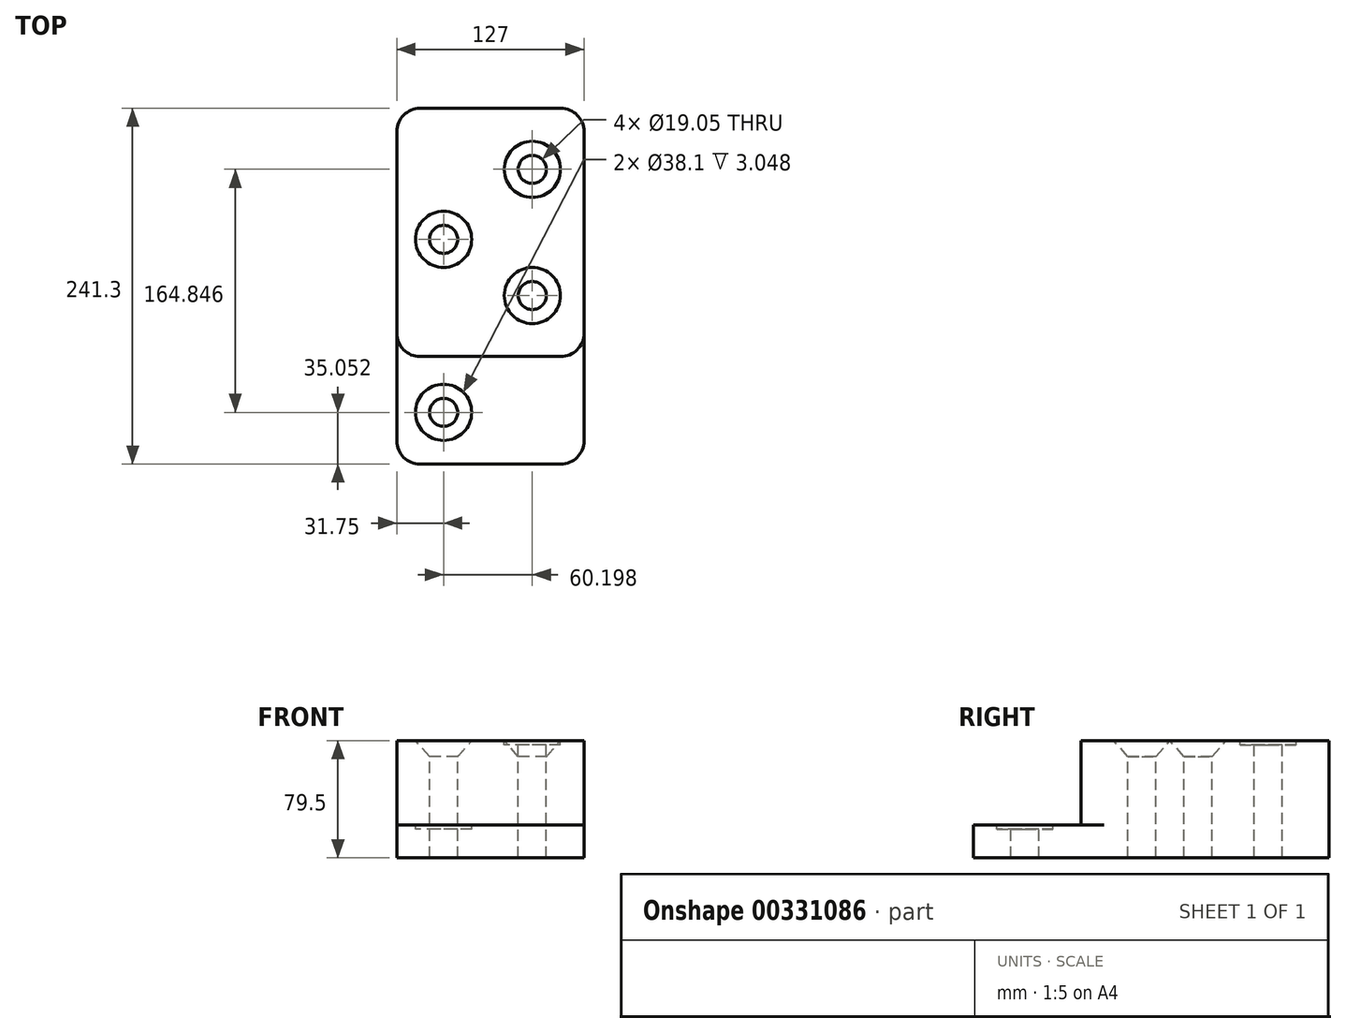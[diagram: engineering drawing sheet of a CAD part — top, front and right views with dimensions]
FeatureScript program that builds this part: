
annotation { "Feature Type Name" : "Feature", "Feature Type Description" : "" }
export const myFeature = defineFeature(function(context is Context, id is Id, definition is map)
    precondition{}
    {
        {
            var Q0;
            Q0=qCreatedBy(makeId("Top.planeOp"),FACE);
            var sketch = newSketch(context, id + "F0", { "sketchPlane" : qUnion([Q0])});
            skLineSegment(sketch, "E0.bottom", {"start": v(0, 0) * mm, "end": v(127, 0) * mm});
            skLineSegment(sketch, "E0.top", {"start": v(0, 241.3) * mm, "end": v(127, 241.3) * mm});
            skLineSegment(sketch, "E0.left", {"start": v(0, 0) * mm, "end": v(0, 241.3) * mm});
            skLineSegment(sketch, "E0.right", {"start": v(127, 0) * mm, "end": v(127, 241.3) * mm});
            skLineSegment(sketch, "E1.top", {"start": v(0, 72.9) * mm, "end": v(127, 72.9) * mm});
            skLineSegment(sketch, "E1.left", {"start": v(0, 241.3) * mm, "end": v(0, 72.9) * mm});
            skLineSegment(sketch, "E1.right", {"start": v(127, 241.3) * mm, "end": v(127, 72.9) * mm});
            skSolve(sketch);
        }
        {
            var Q0;
            Q0=makeQuery(id+"F0.imprint","IMPRINT",FACE,{"disambiguationData":[TD([[makeQuery(id+"F0.imprint","IMPRINT",EDGE,{"derivedFrom":sQuery(id+"F0.wireOp",EDGE,"Odrjzz7N-8wh7-MPak-k5Dz-F2fuVoLMaVHb")}),1.0]])]});
            var Q1;
            Q1=makeQuery(id+"F0.imprint","IMPRINT",FACE,{"disambiguationData":[TD([[makeQuery(id+"F0.imprint","IMPRINT",EDGE,{"derivedFrom":sQuery(id+"F0.wireOp",EDGE,"E0.bottom")}),1.0]])]});
            extrude(context, id + "F1", {"entities" : qUnion([Q0, Q1]), "depth" : 22.35 * mm});
        }
        {
            var Q0;
            Q0=makeQuery(id+"F0.imprint","IMPRINT",FACE,{"disambiguationData":[TD([[makeQuery(id+"F0.imprint","IMPRINT",EDGE,{"derivedFrom":sQuery(id+"F0.wireOp",EDGE,"E0.top")}),-1.0]])]});
            extrude(context, id + "F2", {"entities" : qUnion([Q0]), "operationType" : NewBodyOperationType.ADD, "depth" : 79.5 * mm});
        }
        {
            var Q0;
            Q0=makeQuery(id+"F2.opExtrude","SWEPT_EDGE",EDGE,{"disambiguationData":[OSD([sQuery(id+"F0.wireOp",EDGE,"E0.right"),sQuery(id+"F0.wireOp",EDGE,"E1.top"),sQuery(id+"F0.wireOp",EDGE,"E1.right")])]});
            var Q1;
            Q1=makeQuery(id+"F2.opExtrude","SWEPT_EDGE",EDGE,{"disambiguationData":[OSD([sQuery(id+"F0.wireOp",EDGE,"E0.left"),sQuery(id+"F0.wireOp",EDGE,"E1.top"),sQuery(id+"F0.wireOp",EDGE,"E1.left")])]});
            var Q2;
            Q2=makeQuery(id+"F2.opExtrude","SWEPT_EDGE",EDGE,{"disambiguationData":[OSD([sQuery(id+"F0.wireOp",EDGE,"E0.top"),sQuery(id+"F0.wireOp",EDGE,"E1.right")])]});
            var Q3;
            Q3=makeQuery(id+"F2.opExtrude","SWEPT_EDGE",EDGE,{"disambiguationData":[OSD([sQuery(id+"F0.wireOp",EDGE,"E0.top"),sQuery(id+"F0.wireOp",EDGE,"E1.left")])]});
            var Q4;
            Q4=makeQuery(id+"F1.opExtrude","SWEPT_EDGE",EDGE,{"disambiguationData":[OSD([sQuery(id+"F0.wireOp",EDGE,"E0.bottom"),sQuery(id+"F0.wireOp",EDGE,"E0.right")])]});
            var Q5;
            Q5=makeQuery(id+"F1.opExtrude","SWEPT_EDGE",EDGE,{"disambiguationData":[OSD([sQuery(id+"F0.wireOp",EDGE,"E0.bottom"),sQuery(id+"F0.wireOp",EDGE,"E0.left")])]});
            fillet(context, id + "F3", {"entities" : qUnion([Q0, Q1, Q2, Q3, Q4, Q5]), "radius" : 15.75 * mm, "tangentPropagation" : true, "allowEdgeOverflow" : false});
        }
        {
            var Q0;
            Q0=makeQuery(id+"F1.opExtrude","CAP_FACE",FACE,{"disambiguationData":[OSD([sQuery(id+"F0.wireOp",EDGE,"E0.bottom"),sQuery(id+"F0.wireOp",EDGE,"E0.left"),sQuery(id+"F0.wireOp",EDGE,"E0.right"),sQuery(id+"F0.wireOp",EDGE,"E1.top")])],"isStart":false});
            var sketch = newSketch(context, id + "F4", { "sketchPlane" : qUnion([Q0])});
            skPoint(sketch, "E2", {"position": v(31.75, 35.05) * mm});
            skSolve(sketch);
        }
        {
            var Q0;
            Q0=makeQuery(id+"F2.opExtrude","CAP_FACE",FACE,{"disambiguationData":[OSD([sQuery(id+"F0.wireOp",EDGE,"E0.top"),sQuery(id+"F0.wireOp",EDGE,"E1.top"),sQuery(id+"F0.wireOp",EDGE,"E1.left"),sQuery(id+"F0.wireOp",EDGE,"E1.right")])],"isStart":false});
            var sketch = newSketch(context, id + "F5", { "sketchPlane" : qUnion([Q0])});
            skPoint(sketch, "E3", {"position": v(31.75, 152.4) * mm});
            skPoint(sketch, "E4", {"position": v(91.95, 114.3) * mm});
            skPoint(sketch, "E5", {"position": v(91.95, 199.9) * mm});
            skSolve(sketch);
        }
        {
            var Q0;
            Q0=sQuery(id+"F5.wireOp",VERTEX,"E5");
            var Q1;
            Q1=sQuery(id+"F4.wireOp",VERTEX,"E2");
            var Q2;
            Q2=makeQuery(id+"F1.opExtrude","SWEPT_BODY",BODY,{"disambiguationData":[OSD([sQuery(id+"F0.wireOp",EDGE,"E0.bottom"),sQuery(id+"F0.wireOp",EDGE,"E0.left"),sQuery(id+"F0.wireOp",EDGE,"E0.right"),sQuery(id+"F0.wireOp",EDGE,"E1.top")])]});
            hole(context, id + "F6", {"style" : HoleStyle.C_BORE, "endStyle" : HoleEndStyle.THROUGH, "holeDiameter" : 19.05 * mm, "cBoreDiameter" : 38.1 * mm, "cBoreDepth" : 3.05 * mm, "tappedDepth" : 12.7 * mm, "tapClearance" : 3, "locations" : qUnion([Q0, Q1]), "scope" : qUnion([Q2])});
        }
        {
            var Q0;
            Q0=sQuery(id+"F5.wireOp",VERTEX,"E3");
            var Q1;
            Q1=sQuery(id+"F5.wireOp",VERTEX,"E4");
            var Q2;
            Q2=makeQuery(id+"F1.opExtrude","SWEPT_BODY",BODY,{"disambiguationData":[OSD([sQuery(id+"F0.wireOp",EDGE,"E0.bottom"),sQuery(id+"F0.wireOp",EDGE,"E0.left"),sQuery(id+"F0.wireOp",EDGE,"E0.right"),sQuery(id+"F0.wireOp",EDGE,"E1.top")])]});
            hole(context, id + "F7", {"style" : HoleStyle.C_SINK, "endStyle" : HoleEndStyle.THROUGH, "holeDiameter" : 19.05 * mm, "cSinkDiameter" : 38.1 * mm, "cSinkAngle" : 82 * degree, "tappedDepth" : 12.7 * mm, "tapClearance" : 3, "locations" : qUnion([Q0, Q1]), "scope" : qUnion([Q2])});
        }
    });
